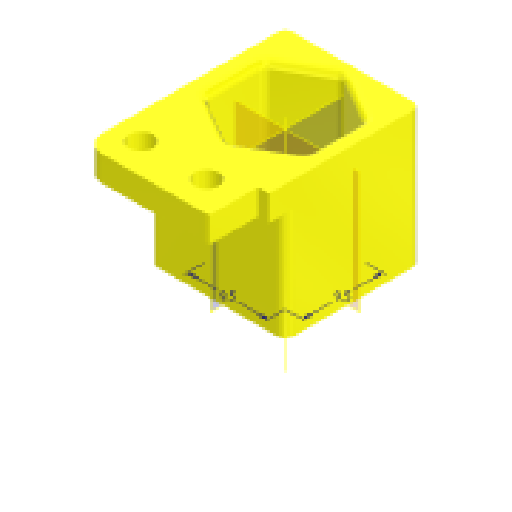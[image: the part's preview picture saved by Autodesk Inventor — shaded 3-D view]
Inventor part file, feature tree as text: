
AUTODESK INVENTOR PART (.ipt)
format: ipt  version: 2024.1 (Build 281209000, 209)  size: 258,560 bytes
history: native  units: mm
features: extrude x4, other x3, sketch x3, projected_geometry x3, fillet x2, plane x2, reference x1
ambient origin geometry x8: Origin, YZ Plane, XZ Plane, XY Plane, X Axis, Y Axis, Z Axis, Center Point
bodies: Volumenkörper1 (feature_tree)
feature tree (18):
  extrude  "Extrusion1"  Depth=16.0mm
  fillet  "Rundung1"  Radius=3.0mm
  extrude  "Extrusion2"  Depth=13.0mm
  fillet  "Rundung2"  Radius=13.0mm
  other  "Arbeitsachse1"
  extrude  "Extrusion3"  Depth=10.0mm
  extrude  "Extrusion4"  Depth=3.0mm
  sketch  "Skizze5"  dims[d9=1.0mm d10=10.0mm d11=2.8mm d12=2.8mm d13=2.0mm d14=3.0mm d15=0.0mm d16=0.1mm d17=0.0mm d18=0.0mm d19=9.5mm d20=9.5mm d21=6.0mm d22=9.5mm d23=9.5mm d24=1.8mm d25=1.8mm d26=1.8mm d27=1.8mm]
  sketch  "Skizze2"  dims[d0=16.0mm d1=16.0mm d3=3.0mm d4=0.0mm]
  projected_geometry  "Projizierte Kontur1"
  plane  "Arbeitsebene1"
  plane  "Arbeitsebene2"
  sketch  "Skizze3"  dims[d5=2.0mm d6=11.85mm d7=13.0mm d8=0.0mm]
  projected_geometry  "Projizierte Kontur2"
  reference  "Referenz1"
  projected_geometry  "Projizierte Kontur3"
  other  "Assemlby_lightsheet_generator_passive_v2.iam"
  other  "30_Lightsheet_generator_passive_lid_v1:1"
